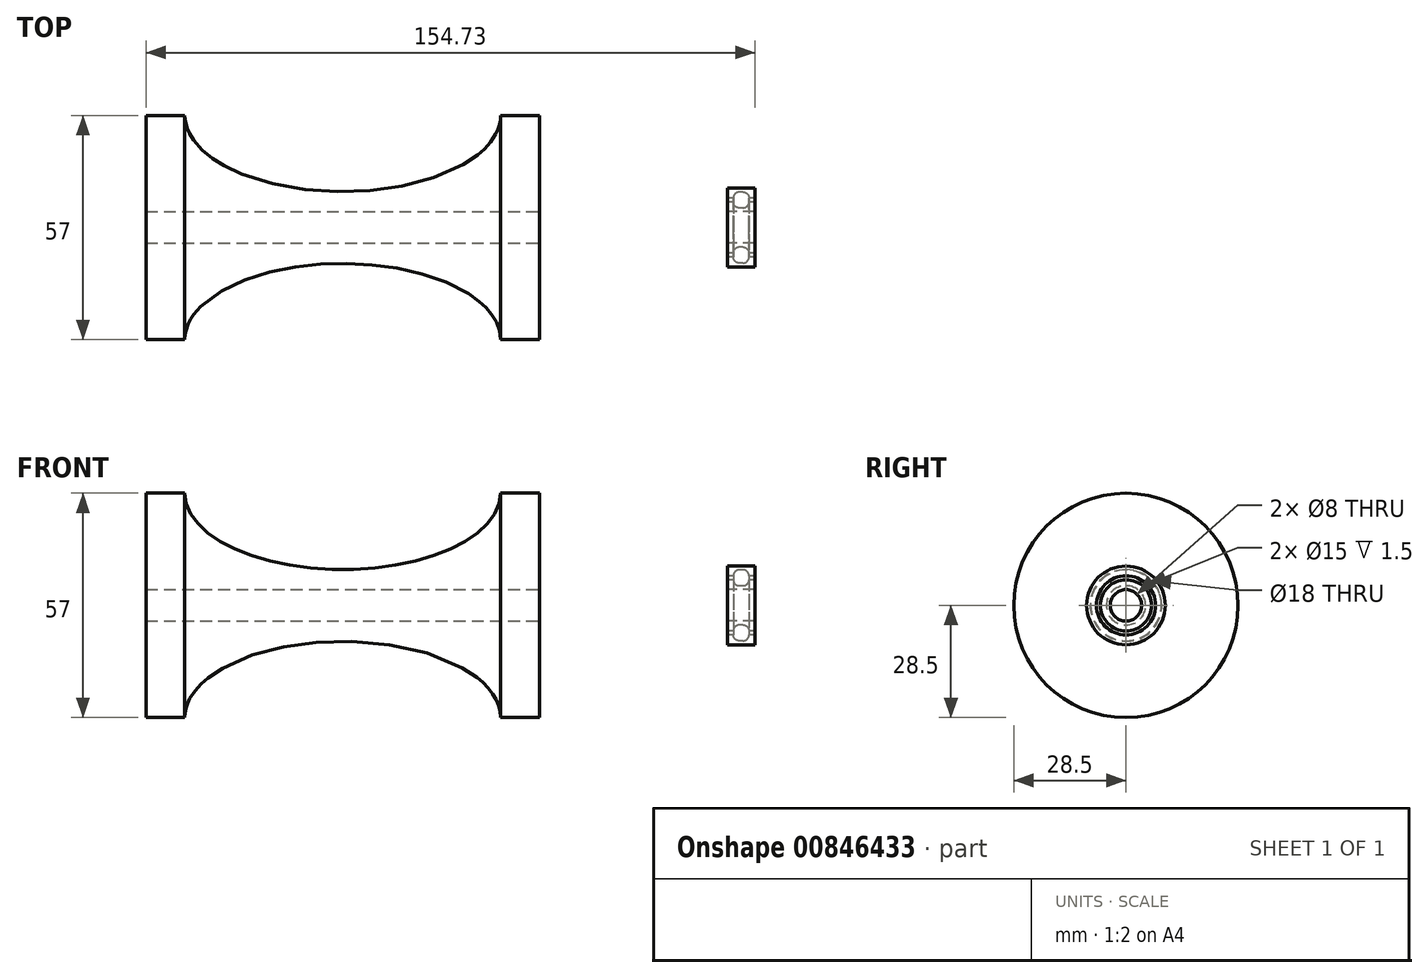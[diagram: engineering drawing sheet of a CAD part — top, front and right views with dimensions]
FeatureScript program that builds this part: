
annotation { "Feature Type Name" : "Feature", "Feature Type Description" : "" }
export const myFeature = defineFeature(function(context is Context, id is Id, definition is map)
    precondition{}
    {
        {
            var Q0;
            Q0=qCreatedBy(makeId("Right.planeOp"),FACE);
            var sketch = newSketch(context, id + "F0", { "sketchPlane" : qUnion([Q0])});
            skCircle(sketch, "E0", {"center": v(0, 0) * mm, "radius": 28.5 * mm});
            skCircle(sketch, "E1", {"center": v(0, 0) * mm, "radius": 4 * mm});
            skSolve(sketch);
        }
        {
            var Q0;
            Q0=makeQuery(id+"F0.imprint","IMPRINT",FACE,{"disambiguationData":[TD([[makeQuery(id+"F0.imprint","IMPRINT",EDGE,{"derivedFrom":sQuery(id+"F0.wireOp",EDGE,"E0")}),1.0]])]});
            extrude(context, id + "F1", {"entities" : qUnion([Q0]), "oppositeDirection" : true, "depth" : 100 * mm, "offsetDistance" : 25 * mm});
        }
        {
            var Q0;
            Q0=qCreatedBy(makeId("Front.planeOp"),FACE);
            var sketch = newSketch(context, id + "F2", { "sketchPlane" : qUnion([Q0])});
            skLineSegment(sketch, "E2.0", {"start": v(-100, 28.5) * mm, "end": v(-100, -28.5) * mm, "construction": true});
            skLineSegment(sketch, "E2.1", {"start": v(0, 28.5) * mm, "end": v(0, -28.5) * mm, "construction": true});
            skLineSegment(sketch, "E3", {"start": v(0, 0) * mm, "end": v(-103.06, 0) * mm, "construction": true});
            skLineSegment(sketch, "E4", {"start": v(0, 9.27) * mm, "end": v(0, -9.73) * mm, "construction": true});
            skLineSegment(sketch, "E5", {"start": v(0, 9.27) * mm, "end": v(-119.48, 9.27) * mm, "construction": true});
            skLineSegment(sketch, "E6", {"start": v(0, -9.73) * mm, "end": v(-117.05, -9.73) * mm, "construction": true});
            skLineSegment(sketch, "E7", {"start": v(0, 31.32) * mm, "end": v(-10, 31.32) * mm, "construction": true});
            skLineSegment(sketch, "E8", {"start": v(-100, 31.69) * mm, "end": v(-90, 31.69) * mm, "construction": true});
            skLineSegment(sketch, "E9", {"start": v(-90, 31.69) * mm, "end": v(-90, -49.4) * mm, "construction": true});
            skLineSegment(sketch, "E10", {"start": v(-10, 31.32) * mm, "end": v(-10, -46.7) * mm, "construction": true});
            skLineSegment(sketch, "E11", {"start": v(-100, 28.5) * mm, "end": v(0, 28.5) * mm, "construction": true});
            skEllipse(sketch, "E12", {"center": v(-50, 28.5) * mm, "majorRadius": 19.36 * mm, "minorRadius": 40.11 * mm, "majorAxis": v(0, -1)});
            skSolve(sketch);
        }
        {
            var Q0;
            Q0=qCreatedBy(makeId("Front.planeOp"),FACE);
            var sketch = newSketch(context, id + "F3", { "sketchPlane" : qUnion([Q0])});
            skLineSegment(sketch, "E13", {"start": v(54.73, 0) * mm, "end": v(54.73, 4) * mm, "construction": true});
            skLineSegment(sketch, "E14", {"start": v(54.73, 4) * mm, "end": v(47.73, 4) * mm});
            skLineSegment(sketch, "E15", {"start": v(47.73, 4) * mm, "end": v(47.73, 6.5) * mm});
            skLineSegment(sketch, "E16", {"start": v(47.73, 6.5) * mm, "end": v(49.23, 6.5) * mm});
            skLineSegment(sketch, "E17", {"start": v(49.23, 6.5) * mm, "end": v(49.23, 6.5) * mm});
            skLineSegment(sketch, "E18", {"start": v(50.73, 5) * mm, "end": v(51.73, 5) * mm});
            skLineSegment(sketch, "E19", {"start": v(53.23, 6.5) * mm, "end": v(53.23, 6.5) * mm});
            skLineSegment(sketch, "E20", {"start": v(53.23, 6.5) * mm, "end": v(54.73, 6.5) * mm});
            skLineSegment(sketch, "E21", {"start": v(54.73, 6.5) * mm, "end": v(54.73, 4) * mm});
            skLineSegment(sketch, "E22", {"start": v(51.23, 4) * mm, "end": v(51.23, 14.1) * mm, "construction": true});
            skArc(sketch, "E23", {"start": v(51.23, 5.3) * mm, "mid": v(52.93, 7) * mm, "end": v(51.23, 8.7) * mm});
            skLineSegment(sketch, "E24", {"start": v(47.8, 5.3) * mm, "end": v(53.23, 5.3) * mm, "construction": true});
            skLineSegment(sketch, "E25", {"start": v(44.7, 7) * mm, "end": v(54.13, 7) * mm, "construction": true});
            skLineSegment(sketch, "E26.MirrorCS", {"start": v(47.73, 10) * mm, "end": v(47.73, 7.5) * mm});
            skLineSegment(sketch, "E27.MirrorCS", {"start": v(47.73, 7.5) * mm, "end": v(49.23, 7.5) * mm});
            skLineSegment(sketch, "E28.MirrorCS", {"start": v(49.23, 7.5) * mm, "end": v(49.23, 7.5) * mm});
            skLineSegment(sketch, "E29.MirrorCS", {"start": v(50.73, 9) * mm, "end": v(51.73, 9) * mm});
            skLineSegment(sketch, "E30.MirrorCS", {"start": v(53.23, 7.5) * mm, "end": v(53.23, 7.5) * mm});
            skLineSegment(sketch, "E31.MirrorCS", {"start": v(53.23, 7.5) * mm, "end": v(54.73, 7.5) * mm});
            skLineSegment(sketch, "E32.MirrorCS", {"start": v(54.73, 7.5) * mm, "end": v(54.73, 10) * mm});
            skLineSegment(sketch, "E33.MirrorCS", {"start": v(54.73, 10) * mm, "end": v(47.73, 10) * mm});
            skLineSegment(sketch, "E34", {"start": v(-72.43, 0) * mm, "end": v(124.56, 0) * mm, "construction": true});
            skLineSegment(sketch, "E35", {"start": v(53.23, 7.5) * mm, "end": v(53.23, 6.5) * mm, "construction": true});
            skPoint(sketch, "E36.visualSharp", {"position": v(49.23, 9) * mm});
            skArc(sketch, "E36.filletArc", {"start": v(50.73, 9) * mm, "mid": v(49.67, 8.56) * mm, "end": v(49.23, 7.5) * mm});
            skPoint(sketch, "E37.visualSharp", {"position": v(53.23, 9) * mm});
            skArc(sketch, "E37.filletArc", {"start": v(53.23, 7.5) * mm, "mid": v(52.8, 8.56) * mm, "end": v(51.73, 9) * mm});
            skPoint(sketch, "E38.visualSharp", {"position": v(49.23, 5) * mm});
            skArc(sketch, "E38.filletArc", {"start": v(49.23, 6.5) * mm, "mid": v(49.67, 5.44) * mm, "end": v(50.73, 5) * mm});
            skPoint(sketch, "E39.visualSharp", {"position": v(53.23, 5) * mm});
            skArc(sketch, "E39.filletArc", {"start": v(51.73, 5) * mm, "mid": v(52.8, 5.44) * mm, "end": v(53.23, 6.5) * mm});
            skSolve(sketch);
        }
        {
            var Q0;
            Q0=makeQuery(id+"F3.imprint","IMPRINT",FACE,{"disambiguationData":[TD([[makeQuery(id+"F3.imprint","IMPRINT",EDGE,{"derivedFrom":sQuery(id+"F3.wireOp",EDGE,"E26.MirrorCS")}),1.0]])]});
            var Q1;
            Q1=makeQuery(id+"F3.imprint","IMPRINT",FACE,{"disambiguationData":[TD([[makeQuery(id+"F3.imprint","IMPRINT",EDGE,{"derivedFrom":sQuery(id+"F3.wireOp",EDGE,"E14")}),-1.0]])]});
            var Q2;
            Q2=sQuery(id+"F3.wireOp",EDGE,"E34");
            revolve(context, id + "F4", {"surfaceOperationType" : NewSurfaceOperationType.NEW, "entities" : qUnion([Q0, Q1]), "axis" : qUnion([Q2]), "revolveType" : RevolveType.FULL});
        }
        {
            var Q0;
            Q0=sQuery(id+"F3.wireOp",EDGE,"E23");
            var Q1;
            Q1=sQuery(id+"F3.wireOp",EDGE,"E22");
            revolve(context, id + "F5", {"bodyType" : ToolBodyType.SURFACE, "surfaceOperationType" : NewSurfaceOperationType.NEW, "surfaceEntities" : qUnion([Q0]), "axis" : qUnion([Q1]), "revolveType" : RevolveType.FULL});
        }
        {
            var Q0;
            Q0=makeQuery(id+"F5.opRevolve","SWEPT_BODY",BODY,{"disambiguationData":[OSD([sQuery(id+"F3.wireOp",EDGE,"E23")])]});
            var Q1;
            Q1=makeQuery(id+"F4.opRevolve","SWEPT_EDGE",EDGE,{"disambiguationData":[OSD([sQuery(id+"F3.wireOp",EDGE,"E14"),sQuery(id+"F3.wireOp",EDGE,"E21")])]});
            circularPattern(context, id + "F6", {"entities" : qUnion([Q0]), "axis" : qUnion([Q1]), "angle" : 360 * degree, "instanceCount" : 12, "equalSpace" : true});
        }
        {
            var Q0;
            Q0=makeQuery(id+"F2.imprint","IMPRINT",FACE,{"disambiguationData":[TD([[makeQuery(id+"F2.imprint","IMPRINT",EDGE,{"derivedFrom":sQuery(id+"F2.wireOp",EDGE,"E12")}),1.0]])]});
            var Q1;
            Q1=sQuery(id+"F2.wireOp",EDGE,"E3");
            revolve(context, id + "F7", {"operationType" : NewBodyOperationType.REMOVE, "surfaceOperationType" : NewSurfaceOperationType.NEW, "entities" : qUnion([Q0]), "axis" : qUnion([Q1]), "revolveType" : RevolveType.FULL, "oppositeDirection" : true});
        }
    });
